# Revit family: Panorama
name_source: partatom
category: Generic Models
units: mm (PartAtom-declared; Revit-internal decimal feet)

## family parameters
Always vertical = Yes
Can host rebar = No
Cut with Voids When Loaded = No
Part Type = Normal
Room Calculation Point = No
Round Connector Dimension = Use Diameter
Shared = No
Work Plane-Based = No

## types (14) — shared parameters
Glass Thickness = 15 mm  [stored 0.0492126 ft]
Hand rail QTY = 2
Hand rail height = 850 mm  [stored 2.78871 ft]
Manufacturer = UNEX SYSTEMS
Max Panel Size = 1400 mm  [stored 4.59318 ft]
Panel QTY = 2
URL = WWW.UNEX.CO.NZ
zero-valued in all types: Default Elevation

## per-type parameters (varying)
- PANORAMA ( No Rails)*Sentry glass only: ARN (Top rail)=Yes; ART (Top rail)=No; ART (side fix)=No; Arena QTY per panel=6; Arena points total=12; C2C=2400 mm  [stored 7.87402 ft]; Description=UNEX PANORAMA FRAMELESS GLASS WITH ARN RAIL; End gap=50 mm  [stored 0.164042 ft]; Glass Height=1356 mm  [stored 4.44882 ft]; Hand rail brackets=No; Hand rail space=1000 mm  [stored 3.28084 ft]; Height=1400 mm  [stored 4.59318 ft]; Keynote=UNEX SYSTEMS, PANORAMA SIDE FIXED BALUSTRADE; LRR ( Side fix Round hand rail)=No; LRS (Top rail)=No; Length=2500 mm  [stored 8.2021 ft]; Model=UNEX, PANORAMA SIDE FIXED WITH TOP (ARN); PRR (Top Rail)=No; PRR(Side fix)=No; Panel Size=1200 mm; VRE (Side fix)=No; VRE (Top rail)=No; VRR (Side fix)=No; VRR (Top rail)=No; VRT (Top rail)=No; VRT(Side fix)=No
- PANORAMA (ARN Top rail): ARN (Top rail)=Yes; ART (Top rail)=No; ART (side fix)=No; Arena QTY per panel=6; Arena points total=12; C2C=2400 mm  [stored 7.87402 ft]; Description=UNEX PANORAMA FRAMELESS GLASS WITH ARN RAIL; End gap=50 mm  [stored 0.164042 ft]; Glass Height=1156 mm  [stored 3.79265 ft]; Hand rail brackets=No; Hand rail space=1000 mm  [stored 3.28084 ft]; Height=1200 mm; Keynote=UNEX SYSTEMS, PANORAMA SIDE FIXED BALUSTRADE; LRR ( Side fix Round hand rail)=No; LRS (Top rail)=No; Length=2500 mm  [stored 8.2021 ft]; Model=UNEX, PANORAMA SIDE FIXED WITH TOP (ARN); PRR (Top Rail)=No; PRR(Side fix)=No; Panel Size=1200 mm; VRE (Side fix)=No; VRE (Top rail)=No; VRR (Side fix)=No; VRR (Top rail)=No; VRT (Top rail)=No; VRT(Side fix)=No
- PANORAMA (ART Top rail): ARN (Top rail)=No; ART (Top rail)=Yes; ART (side fix)=No; Arena QTY per panel=6; Arena points total=12; C2C=2400 mm  [stored 7.87402 ft]; Description=UNEX PANORAMA FRAMELESS GLASS WITH ART TOP RAIL; End gap=50 mm  [stored 0.164042 ft]; Glass Height=1174 mm; Hand rail brackets=No; Hand rail space=1000 mm  [stored 3.28084 ft]; Height=1218 mm  [stored 3.99606 ft]; Keynote=UNEX SYSTEMS, PANORAMA SIDE FIXED BALUSTRADE; LRR ( Side fix Round hand rail)=No; LRS (Top rail)=No; Length=2500 mm  [stored 8.2021 ft]; Model=UNEX, PANORAMA SIDE FIXED WITH TOP (ART); PRR (Top Rail)=No; PRR(Side fix)=No; Panel Size=1200 mm; VRE (Side fix)=No; VRE (Top rail)=No; VRR (Side fix)=No; VRR (Top rail)=No; VRT (Top rail)=No; VRT(Side fix)=No
- PANORAMA (PRR Top rail): ARN (Top rail)=No; ART (Top rail)=No; ART (side fix)=No; Arena QTY per panel=6; Arena points total=12; C2C=2400 mm  [stored 7.87402 ft]; Description=UNEX METROPOLIS FRAMELESS GLASS WITH……  RAIL

UNEX PANORAMA FRAMELESS GLASS WITH PRR TOP RAIL; End gap=50 mm  [stored 0.164042 ft]; Glass Height=1174 mm; Hand rail brackets=No; Hand rail space=1000 mm  [stored 3.28084 ft]; Height=1218 mm  [stored 3.99606 ft]; Keynote=UNEX SYSTEMS, PANORAMA SIDE FIXED BALUSTRADE; LRR ( Side fix Round hand rail)=No; LRS (Top rail)=No; Length=2500 mm  [stored 8.2021 ft]; Model=UNEX, PANORAMA SIDE FIXED WITH TOP (PRR); PRR (Top Rail)=Yes; PRR(Side fix)=No; Panel Size=1200 mm; VRE (Side fix)=No; VRE (Top rail)=No; VRR (Side fix)=No; VRR (Top rail)=No; VRT (Top rail)=No; VRT(Side fix)=No
- PANORAMA (VRE Top rail): ARN (Top rail)=No; ART (Top rail)=No; ART (side fix)=No; Arena QTY per panel=6; Arena points total=12; C2C=2400 mm  [stored 7.87402 ft]; Description=UNEX PANORAMA FRAMELESS GLASS WITH VRE TOP RAIL; End gap=50 mm  [stored 0.164042 ft]; Glass Height=1174 mm; Hand rail brackets=No; Hand rail space=1000 mm  [stored 3.28084 ft]; Height=1218 mm  [stored 3.99606 ft]; Keynote=UNEX SYSTEMS, PANORAMA SIDE FIXED BALUSTRADE; LRR ( Side fix Round hand rail)=No; LRS (Top rail)=No; Length=2500 mm  [stored 8.2021 ft]; Model=UNEX, PANORAMA SIDE FIXED WITH TOP (VRE); PRR (Top Rail)=No; PRR(Side fix)=No; Panel Size=1200 mm; VRE (Side fix)=No; VRE (Top rail)=Yes; VRR (Side fix)=No; VRR (Top rail)=No; VRT (Top rail)=No; VRT(Side fix)=No
- PANORAMA (VRR Top rail): ARN (Top rail)=No; ART (Top rail)=No; ART (side fix)=No; Arena QTY per panel=6; Arena points total=12; C2C=2500 mm  [stored 8.2021 ft]; Description=UNEX PANORAMA FRAMELESS GLASS WITH VRR TOP RAIL; End gap=0 mm  [stored 0 ft]; Glass Height=1174 mm; Hand rail brackets=No; Hand rail space=1050 mm  [stored 3.44488 ft]; Height=1218 mm  [stored 3.99606 ft]; Keynote=UNEX SYSTEMS, PANORAMA SIDE FIXED BALUSTRADE; LRR ( Side fix Round hand rail)=No; LRS (Top rail)=No; Length=2500 mm  [stored 8.2021 ft]; Model=UNEX, PANORAMA SIDE FIXED WITH TOP (VRR); PRR (Top Rail)=No; PRR(Side fix)=No; Panel Size=1250 mm  [stored 4.10105 ft]; VRE (Side fix)=No; VRE (Top rail)=No; VRR (Side fix)=No; VRR (Top rail)=Yes; VRT (Top rail)=No; VRT(Side fix)=No
- PANORAMA (VRT Top rail): ARN (Top rail)=No; ART (Top rail)=No; ART (side fix)=No; Arena QTY per panel=6; Arena points total=12; C2C=2400 mm  [stored 7.87402 ft]; Description=UNEX PANORAMA FRAMELESS GLASS WITH VRT TOP RAIL; End gap=50 mm  [stored 0.164042 ft]; Glass Height=1174 mm; Hand rail brackets=No; Hand rail space=1000 mm  [stored 3.28084 ft]; Height=1218 mm  [stored 3.99606 ft]; Keynote=UNEX SYSTEMS, PANORAMA SIDE FIXED BALUSTRADE; LRR ( Side fix Round hand rail)=No; LRS (Top rail)=No; Length=2500 mm  [stored 8.2021 ft]; Model=UNEX, PANORAMA SIDE FIXED WITH TOP (VRT); PRR (Top Rail)=No; PRR(Side fix)=No; Panel Size=1200 mm; VRE (Side fix)=No; VRE (Top rail)=No; VRR (Side fix)=No; VRR (Top rail)=No; VRT (Top rail)=Yes; VRT(Side fix)=No
- PANORAMA ( LRR Side rail) *Sentry glass only: ARN (Top rail)=No; ART (Top rail)=No; ART (side fix)=No; Arena QTY per panel=6; Arena points total=12; C2C=2400 mm  [stored 7.87402 ft]; Description=UNEX PANORAMA FRAMELESS SENTRY GLASS WITH LRR SIDE RAIL; End gap=50 mm  [stored 0.164042 ft]; Glass Height=1174 mm; Hand rail brackets=Yes; Hand rail space=1000 mm  [stored 3.28084 ft]; Height=1218 mm  [stored 3.99606 ft]; Keynote=UNEX SYSTEMS, PANORAMA SIDE FIXED BALUSTRADE; LRR ( Side fix Round hand rail)=Yes; LRS (Top rail)=No; Length=2500 mm  [stored 8.2021 ft]; Model=UNEX, PANORAMA SIDE FIXED (LRR SIDE RAIL); PRR (Top Rail)=No; PRR(Side fix)=No; Panel Size=1200 mm; VRE (Side fix)=No; VRE (Top rail)=No; VRR (Side fix)=No; VRR (Top rail)=No; VRT (Top rail)=No; VRT(Side fix)=No
- PANORAMA (LRS Top rail): ARN (Top rail)=No; ART (Top rail)=No; ART (side fix)=No; Arena QTY per panel=7; Arena points total=14; C2C=2700 mm  [stored 8.85827 ft]; Description=UNEX PANORAMA FRAMELESS GLASS WITH LRS TOP RAIL; End gap=50 mm  [stored 0.164042 ft]; Glass Height=1174 mm; Hand rail brackets=No; Hand rail space=1150 mm; Height=1218 mm  [stored 3.99606 ft]; Keynote=UNEX SYSTEMS, PANORAMA SIDE FIXED BALUSTRADE; LRR ( Side fix Round hand rail)=No; LRS (Top rail)=Yes; Length=2800 mm  [stored 9.18635 ft]; Model=UNEX, PANORAMA SIDE FIXED WITH TOP (LRS); PRR (Top Rail)=No; PRR(Side fix)=No; Panel Size=1350 mm  [stored 4.42913 ft]; VRE (Side fix)=No; VRE (Top rail)=No; VRR (Side fix)=No; VRR (Top rail)=No; VRT (Top rail)=No; VRT(Side fix)=No
- PANORAMA (ART Side fix)*Sentry glass only: ARN (Top rail)=No; ART (Top rail)=No; ART (side fix)=Yes; Arena QTY per panel=6; Arena points total=12; C2C=2400 mm  [stored 7.87402 ft]; Description=UNEX PANORAMA FRAMELESS SENTRY GLASS WITH ART SIDE RAIL; End gap=50 mm  [stored 0.164042 ft]; Glass Height=1174 mm; Hand rail brackets=Yes; Hand rail space=1000 mm  [stored 3.28084 ft]; Height=1218 mm  [stored 3.99606 ft]; Keynote=UNEX SYSTEMS, PANORAMA  SIDE FIXED BALUSTRADE; LRR ( Side fix Round hand rail)=No; LRS (Top rail)=No; Length=2500 mm  [stored 8.2021 ft]; Model=UNEX, PANORAMA SIDE FIXED WITH SIDE (ART); PRR (Top Rail)=No; PRR(Side fix)=No; Panel Size=1200 mm; VRE (Side fix)=No; VRE (Top rail)=No; VRR (Side fix)=No; VRR (Top rail)=No; VRT (Top rail)=No; VRT(Side fix)=No
- PANORAMA (PRR Side fix)*Sentry glass only: ARN (Top rail)=No; ART (Top rail)=No; ART (side fix)=No; Arena QTY per panel=6; Arena points total=12; C2C=2400 mm  [stored 7.87402 ft]; Description=UNEX PANORAMA FRAMELESS SENTRY GLASS WITH PRR RAIL; End gap=50 mm  [stored 0.164042 ft]; Glass Height=1174 mm; Hand rail brackets=Yes; Hand rail space=1000 mm  [stored 3.28084 ft]; Height=1218 mm  [stored 3.99606 ft]; Keynote=UNEX SYSTEMS, PANORAMA SIDE FIXED BALUSTRADE; LRR ( Side fix Round hand rail)=No; LRS (Top rail)=No; Length=2500 mm  [stored 8.2021 ft]; Model=UNEX, PANORAMA SIDE FIXED WITH SIDE (PRR); PRR (Top Rail)=No; PRR(Side fix)=Yes; Panel Size=1200 mm; VRE (Side fix)=No; VRE (Top rail)=No; VRR (Side fix)=No; VRR (Top rail)=No; VRT (Top rail)=No; VRT(Side fix)=No
- PANORAMA ( VRE side rail )*Sentry glass only: ARN (Top rail)=No; ART (Top rail)=No; ART (side fix)=No; Arena QTY per panel=6; Arena points total=12; C2C=2400 mm  [stored 7.87402 ft]; Description=UNEX PANORAMA FRAMELESS SENTRY GLASS WITH VRE RAIL; End gap=50 mm  [stored 0.164042 ft]; Glass Height=1174 mm; Hand rail brackets=Yes; Hand rail space=1000 mm  [stored 3.28084 ft]; Height=1218 mm  [stored 3.99606 ft]; Keynote=UNEX SYSTEMS, PANORAMA SIDE FIXED BALUSTRADE; LRR ( Side fix Round hand rail)=No; LRS (Top rail)=No; Length=2500 mm  [stored 8.2021 ft]; Model=UNEX, PANORAMA SIDE FIXED WITH SIDE  (VRE); PRR (Top Rail)=No; PRR(Side fix)=No; Panel Size=1200 mm; VRE (Side fix)=Yes; VRE (Top rail)=No; VRR (Side fix)=No; VRR (Top rail)=No; VRT (Top rail)=No; VRT(Side fix)=No
- PANORAMA ( VRR side rail )*Sentry glass only: ARN (Top rail)=No; ART (Top rail)=No; ART (side fix)=No; Arena QTY per panel=6; Arena points total=12; C2C=2400 mm  [stored 7.87402 ft]; Description=UNEX PANORAMA FRAMELESS SENTRY GLASS WITH VRR SIDE RAIL; End gap=50 mm  [stored 0.164042 ft]; Glass Height=1174 mm; Hand rail brackets=Yes; Hand rail space=1000 mm  [stored 3.28084 ft]; Height=1218 mm  [stored 3.99606 ft]; Keynote=UNEX SYSTEMS, PANORAMA SIDE FIXED BALUSTRADE; LRR ( Side fix Round hand rail)=No; LRS (Top rail)=No; Length=2500 mm  [stored 8.2021 ft]; Model=UNEX, PANORAMA SIDE FIXED WITH SIDE (VRR); PRR (Top Rail)=No; PRR(Side fix)=No; Panel Size=1200 mm; VRE (Side fix)=No; VRE (Top rail)=No; VRR (Side fix)=Yes; VRR (Top rail)=No; VRT (Top rail)=No; VRT(Side fix)=No
- PANORAMA ( VRT side rail )*Sentry glass only: ARN (Top rail)=No; ART (Top rail)=No; ART (side fix)=No; Arena QTY per panel=6; Arena points total=12; C2C=2400 mm  [stored 7.87402 ft]; Description=UNEX PANORAMA FRAMELESS  SENTRY GLASS WITH VRT SIDE RAIL; End gap=50 mm  [stored 0.164042 ft]; Glass Height=1174 mm; Hand rail brackets=Yes; Hand rail space=1000 mm  [stored 3.28084 ft]; Height=1218 mm  [stored 3.99606 ft]; Keynote=UNEX SYSTEMS,PANORAMA SIDE FIXED BALUSTRADE; LRR ( Side fix Round hand rail)=No; LRS (Top rail)=No; Length=2500 mm  [stored 8.2021 ft]; Model=UNEX, PANORAMA  SIDE FIXED WITH SIDE (VRT); PRR (Top Rail)=No; PRR(Side fix)=No; Panel Size=1200 mm; VRE (Side fix)=No; VRE (Top rail)=No; VRR (Side fix)=No; VRR (Top rail)=No; VRT (Top rail)=No; VRT(Side fix)=Yes

note: [stored X ft] marks values corroborated as IEEE doubles in the binary element streams (Revit-internal decimal feet)

## geometry (parser evidence)
native form markers: Sweep x35
no freeform markers — native parametric forms only
